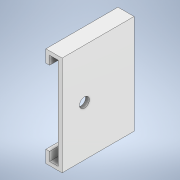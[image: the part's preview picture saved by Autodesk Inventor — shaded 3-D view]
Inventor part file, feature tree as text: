
AUTODESK INVENTOR PART (.ipt)
format: ipt  version: 2021 (Build 250183000, 183)  size: 121,344 bytes
history: native  units: mm
features: extrude x3, sketch x3
ambient origin geometry x8: Origin, YZ Plane, XZ Plane, XY Plane, X Axis, Y Axis, Z Axis, Center Point
bodies: Solid1 (feature_tree)
feature tree (6):
  extrude  "Extrusion1"  Depth=13.0mm
  extrude  "Extrusion2"  Depth=3.0mm
  extrude  "Extrusion3"  Depth=3.0mm
  sketch  "Sketch1"  dims[d0=80.0mm d1=13.0mm]
  sketch  "Sketch2"  dims[d2=58.0mm d3=0.0mm d4=3.0mm]
  sketch  "Sketch3"  dims[d5=3.0mm d6=3.0mm d7=3.0mm d8=10.0mm d9=10.0mm d10=0.0mm d11=0.0mm d12=8.0mm d14=40.0mm d15=0.0mm d16=0.0mm d17=40.0mm]
